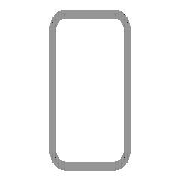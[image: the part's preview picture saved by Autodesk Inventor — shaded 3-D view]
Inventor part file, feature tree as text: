
AUTODESK INVENTOR PART (.ipt)
format: ipt  version: 2025 (Build 290162010, 162A)  size: 129,536 bytes
history: native  units: mm (DEFAULTED — no unit token found)
features: other x4, sketch x1, plane x1
ambient origin geometry x8: Origin, YZ Plane, XZ Plane, XY Plane, X Axis, Y Axis, Z Axis, Center Point
bodies: Solid1 (feature_tree), Body (feature_tree)
feature tree (6):
  parser-record x1  (decoder bookkeeping rows leaked as tree rows — omitted from the tree; the rows remain in map.json)
  other  "Driven Length"
  other  "Start Plane"
  other  "End Plane"
  sketch  "Sketch3"  dims[d3=2000.0mm d4=0.0mm d7=6.0mm d9=40.0mm d11=80.0mm d12=3.0mm d13=-0.0mm d14=2000.0mm d15=20.0mm d16=40.0mm d17=90.0deg d18=2000.0mm]
  plane  "Work Plane3"
